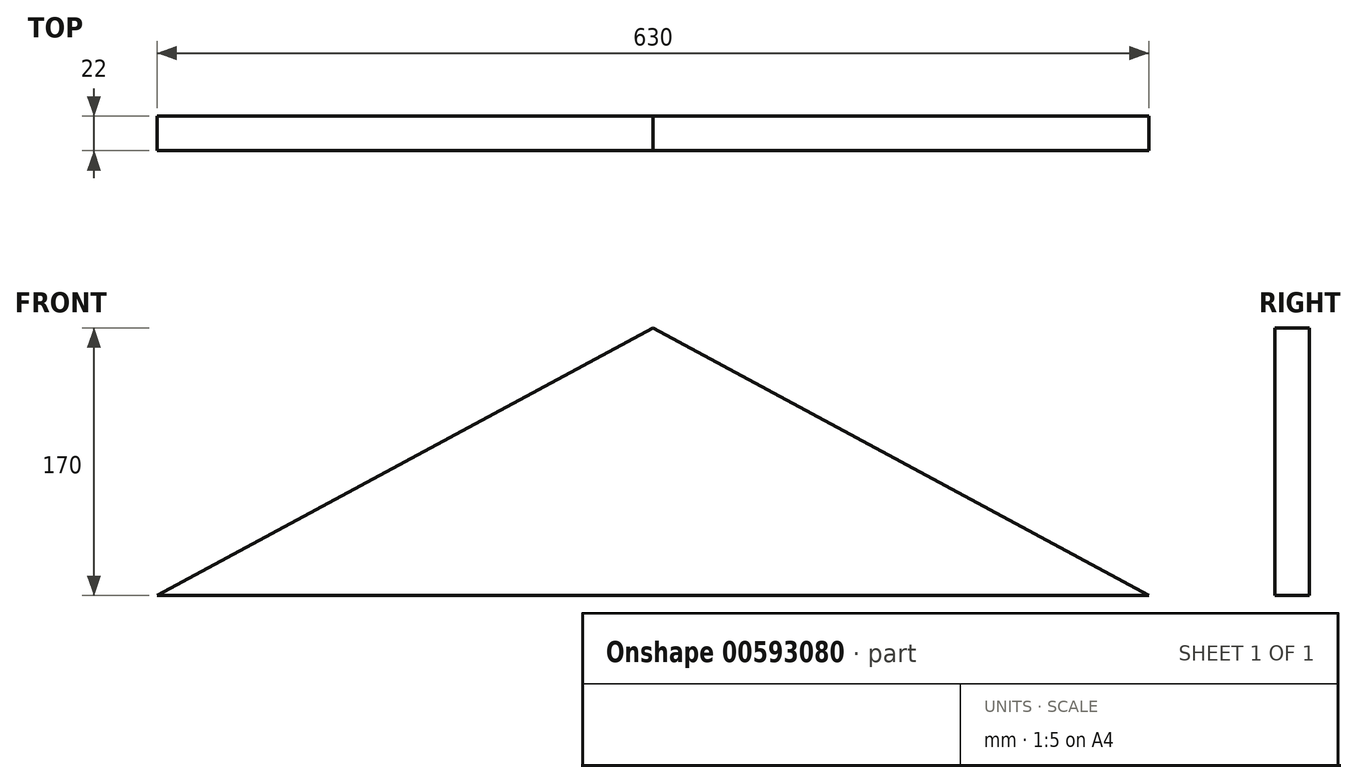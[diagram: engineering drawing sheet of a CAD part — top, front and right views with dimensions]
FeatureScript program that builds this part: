
annotation { "Feature Type Name" : "Feature", "Feature Type Description" : "" }
export const myFeature = defineFeature(function(context is Context, id is Id, definition is map)
    precondition{}
    {
        {
            var Q0;
            Q0=qCreatedBy(makeId("Front.planeOp"),FACE);
            var sketch = newSketch(context, id + "F0", { "sketchPlane" : qUnion([Q0])});
            skLineSegment(sketch, "E0", {"start": v(-315, 0) * mm, "end": v(315, 0) * mm});
            skLineSegment(sketch, "E1", {"start": v(315, 0) * mm, "end": v(0, 170) * mm});
            skLineSegment(sketch, "E2", {"start": v(0, 170) * mm, "end": v(-315, 0) * mm});
            skSolve(sketch);
        }
        {
            var Q0;
            Q0=makeQuery(id+"F0.imprint","IMPRINT",FACE,{"disambiguationData":[TD([[makeQuery(id+"F0.imprint","IMPRINT",EDGE,{"derivedFrom":sQuery(id+"F0.wireOp",EDGE,"E0")}),1.0]])]});
            extrude(context, id + "F1", {"entities" : qUnion([Q0]), "depth" : 22 * mm, "offsetDistance" : 25 * mm});
        }
    });
